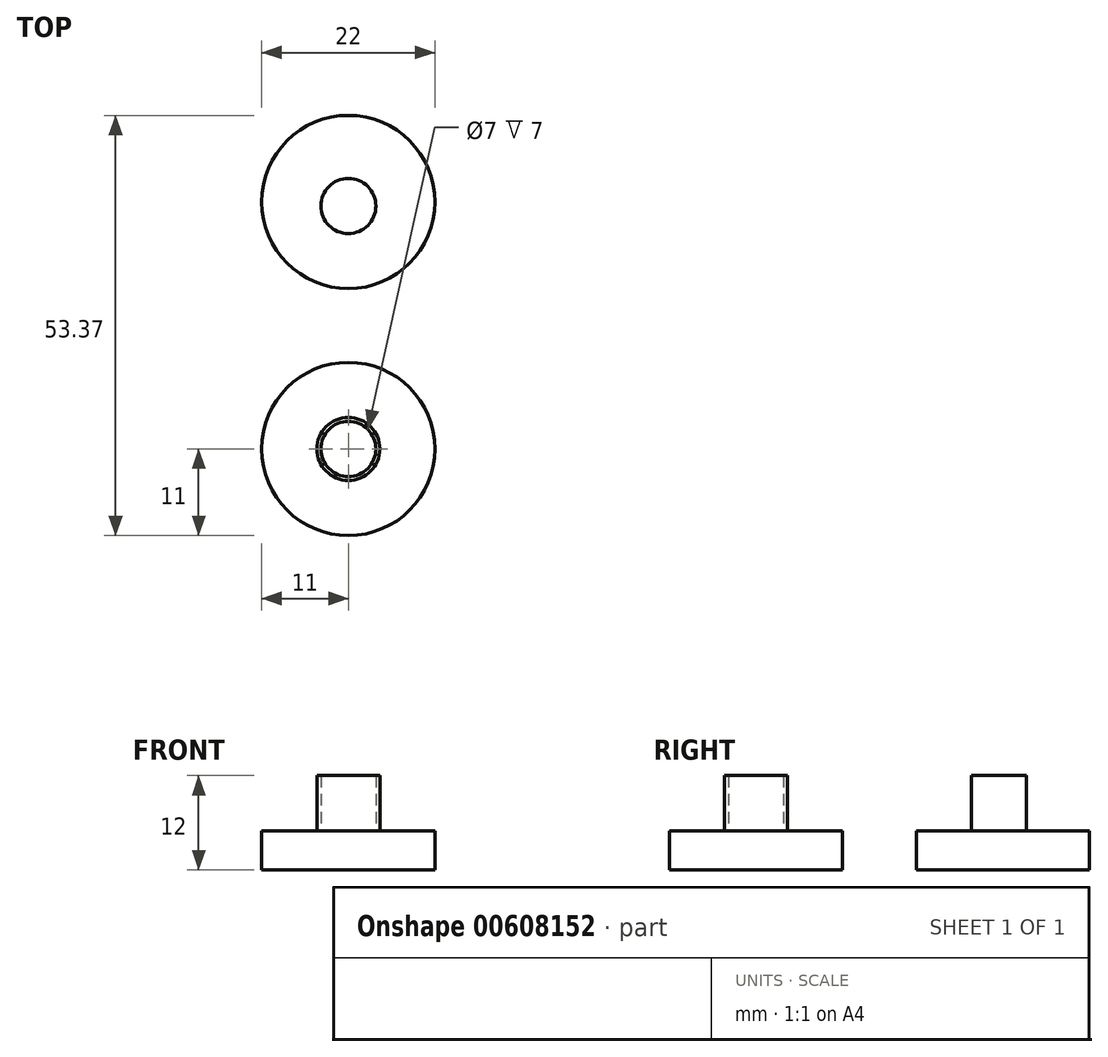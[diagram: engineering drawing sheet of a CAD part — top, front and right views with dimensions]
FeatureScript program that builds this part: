
annotation { "Feature Type Name" : "Feature", "Feature Type Description" : "" }
export const myFeature = defineFeature(function(context is Context, id is Id, definition is map)
    precondition{}
    {
        {
            var Q0;
            Q0=qCreatedBy(makeId("Top.planeOp"),FACE);
            var sketch = newSketch(context, id + "F0", { "sketchPlane" : qUnion([Q0])});
            skCircle(sketch, "E0", {"center": v(0, 0) * mm, "radius": 11 * mm});
            skSolve(sketch);
        }
        {
            var Q0;
            Q0 = qSketchRegion(id + "F0", true);
            extrude(context, id + "F1", {"entities" : qUnion([Q0]), "depth" : 5 * mm, "offsetDistance" : 25 * mm});
        }
        {
            var Q0;
            Q0=makeQuery(id+"F1.opExtrude","CAP_FACE",FACE,{"disambiguationData":[OSD([sQuery(id+"F0.wireOp",EDGE,"E0")])],"isStart":false});
            var sketch = newSketch(context, id + "F2", { "sketchPlane" : qUnion([Q0])});
            skCircle(sketch, "E1", {"center": v(0, 0) * mm, "radius": 4 * mm});
            skCircle(sketch, "E2", {"center": v(0, 0) * mm, "radius": 3.5 * mm});
            skSolve(sketch);
        }
        {
            var Q0;
            Q0 = qSketchRegion(id + "F2", true);
            extrude(context, id + "F3", {"entities" : qUnion([Q0]), "operationType" : NewBodyOperationType.ADD, "depth" : 7 * mm, "offsetDistance" : 25 * mm});
        }
        {
            var Q0;
            Q0=qCreatedBy(makeId("Top.planeOp"),FACE);
            var sketch = newSketch(context, id + "F4", { "sketchPlane" : qUnion([Q0])});
            skCircle(sketch, "E3", {"center": v(0, 31.37) * mm, "radius": 11 * mm});
            skSolve(sketch);
        }
        {
            var Q0;
            Q0 = qSketchRegion(id + "F4", true);
            extrude(context, id + "F5", {"entities" : qUnion([Q0]), "depth" : 5 * mm, "offsetDistance" : 25 * mm});
        }
        {
            var Q0;
            Q0=qCreatedBy(makeId("Top.planeOp"),FACE);
            var sketch = newSketch(context, id + "F6", { "sketchPlane" : qUnion([Q0])});
            skCircle(sketch, "E4", {"center": v(0, 30.86) * mm, "radius": 3.5 * mm});
            skSolve(sketch);
        }
        {
            var Q0;
            Q0 = qSketchRegion(id + "F6", true);
            extrude(context, id + "F7", {"entities" : qUnion([Q0]), "operationType" : NewBodyOperationType.ADD, "depth" : 12 * mm, "offsetDistance" : 25 * mm});
        }
    });
